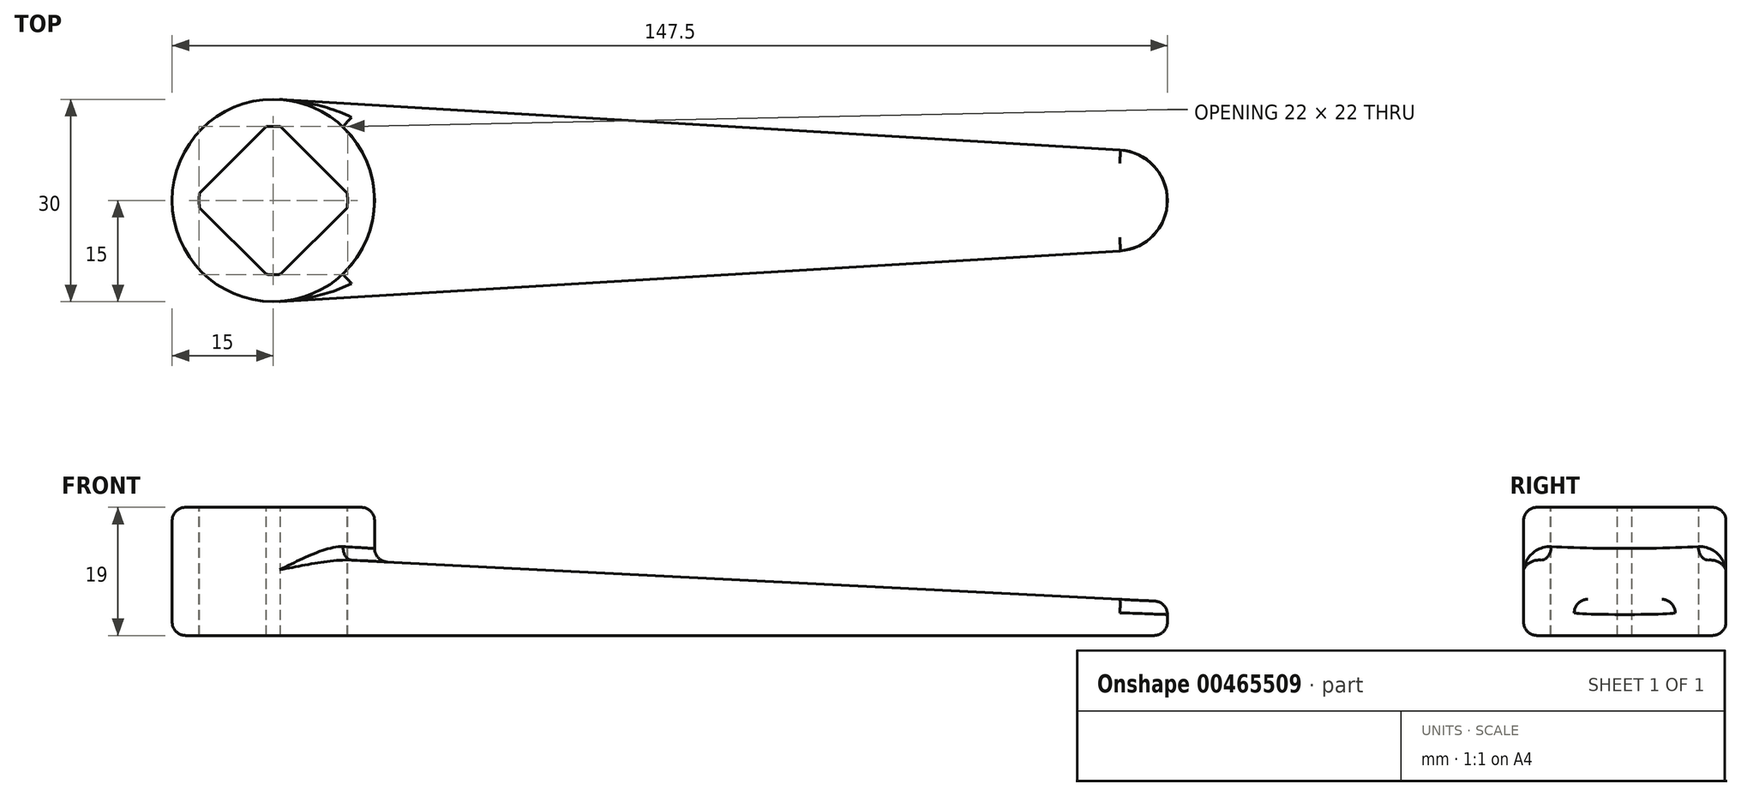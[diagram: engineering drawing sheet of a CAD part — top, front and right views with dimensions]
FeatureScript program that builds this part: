
annotation { "Feature Type Name" : "Feature", "Feature Type Description" : "" }
export const myFeature = defineFeature(function(context is Context, id is Id, definition is map)
    precondition{}
    {
        {
            var Q0;
            Q0=qCreatedBy(makeId("Top.planeOp"),FACE);
            var sketch = newSketch(context, id + "F0", { "sketchPlane" : qUnion([Q0])});
            skCircle(sketch, "E0", {"center": v(0, 0) * mm, "radius": 15 * mm});
            skLineSegment(sketch, "E1", {"start": v(0, 0) * mm, "end": v(125, 0) * mm, "construction": true});
            skCircle(sketch, "E2", {"center": v(125, 0) * mm, "radius": 7.5 * mm});
            skLineSegment(sketch, "E3", {"start": v(0.9, 14.97) * mm, "end": v(125.45, 7.49) * mm});
            skLineSegment(sketch, "E4.MirrorCS", {"start": v(0.9, -14.97) * mm, "end": v(125.45, -7.49) * mm});
            skSolve(sketch);
        }
        {
            var Q0;
            Q0 = qSketchRegion(id + "F0", true);
            extrude(context, id + "F1", {"entities" : qUnion([Q0]), "depth" : 19 * mm});
        }
        {
            var Q0;
            Q0=qCreatedBy(makeId("Front.planeOp"),FACE);
            var sketch = newSketch(context, id + "F2", { "sketchPlane" : qUnion([Q0])});
            skLineSegment(sketch, "E5.0", {"start": v(0.9, 19) * mm, "end": v(125.45, 19) * mm});
            skLineSegment(sketch, "E6.0", {"start": v(0.9, 0) * mm, "end": v(125.45, 0) * mm});
            skLineSegment(sketch, "E7", {"start": v(15, 0) * mm, "end": v(15, 19) * mm});
            skLineSegment(sketch, "E8.0", {"start": v(125.45, 19) * mm, "end": v(132.5, 19) * mm});
            skLineSegment(sketch, "E9", {"start": v(132.5, 19) * mm, "end": v(132.5, 0) * mm});
            skLineSegment(sketch, "E10.0", {"start": v(125.45, 0) * mm, "end": v(132.5, 0) * mm});
            skLineSegment(sketch, "E11", {"start": v(-15, 12.53) * mm, "end": v(132.5, 5) * mm});
            skLineSegment(sketch, "E12", {"start": v(-15, 0) * mm, "end": v(-15, 19) * mm});
            skLineSegment(sketch, "E13.0", {"start": v(0.9, 19) * mm, "end": v(-15, 19) * mm});
            skLineSegment(sketch, "E14.0", {"start": v(0.9, 0) * mm, "end": v(-15, 0) * mm});
            skPoint(sketch, "E15.orphan", {"position": v(15, 11) * mm});
            skSolve(sketch);
        }
        {
            var Q0;
            {var subQ0=sQuery(id+"F2.wireOp",EDGE,"E8.0");Q0=makeQuery(id+"F2.imprint","IMPRINT",FACE,{"disambiguationData":[TD([[makeQuery(id+"F2.imprint","IMPRINT",EDGE,{"derivedFrom":subQ0}),-1.0]])]});}
            var Q1;
            {var subQ3=sQuery(id+"F2.wireOp",EDGE,"E13.0");Q1=makeQuery(id+"F2.imprint","IMPRINT",FACE,{"disambiguationData":[TD([[makeQuery(id+"F2.imprint","IMPRINT",EDGE,{"derivedFrom":subQ3}),1.0]])]});}
            extrude(context, id + "F3", {"entities" : qUnion([Q0, Q1]), "operationType" : NewBodyOperationType.REMOVE, "oppositeDirection" : true, "depth" : 30 * mm, "symmetric" : true});
        }
        {
            var Q0;
            Q0=makeQuery(id+"F1.opExtrude","CAP_FACE",FACE,{"disambiguationData":[OSD([sQuery(id+"F0.wireOp",EDGE,"E0"),sQuery(id+"F0.wireOp",EDGE,"E2"),sQuery(id+"F0.wireOp",EDGE,"E3"),sQuery(id+"F0.wireOp",EDGE,"E4.MirrorCS")])],"isStart":true});
            var sketch = newSketch(context, id + "F4", { "sketchPlane" : qUnion([Q0])});
            skCircle(sketch, "E16", {"center": v(0, 0) * mm, "radius": 15 * mm});
            skSolve(sketch);
        }
        {
            var Q0;
            Q0 = qSketchRegion(id + "F4", true);
            extrude(context, id + "F5", {"entities" : qUnion([Q0]), "operationType" : NewBodyOperationType.ADD, "oppositeDirection" : true, "depth" : 19 * mm});
        }
        {
            var Q0;
            Q0=makeQuery(id+"F5.opExtrude","CAP_FACE",FACE,{"disambiguationData":[OSD([sQuery(id+"F4.wireOp",EDGE,"E16")])],"isStart":false});
            var sketch = newSketch(context, id + "F6", { "sketchPlane" : qUnion([Q0])});
            skCircle(sketch, "E17", {"center": v(0, 0) * mm, "radius": 11 * mm});
            skCircle(sketch, "E18.cCircle", {"center": v(0, 0) * mm, "radius": 12.02 * mm, "construction": true});
            skLineSegment(sketch, "E18.0", {"start": v(0, 12.02) * mm, "end": v(12.02, 0) * mm});
            skLineSegment(sketch, "E18.1", {"start": v(12.02, 0) * mm, "end": v(0, -12.02) * mm});
            skLineSegment(sketch, "E18.2", {"start": v(0, -12.02) * mm, "end": v(-12.02, 0) * mm});
            skLineSegment(sketch, "E18.3", {"start": v(-12.02, 0) * mm, "end": v(0, 12.02) * mm});
            skSolve(sketch);
        }
        {
            var Q0;
            {var subQ0=sQuery(id+"F6.wireOp",EDGE,"E18.0");var subQ1=sQuery(id+"F6.wireOp",EDGE,"E17");var subQ12=makeQuery(id+"F6.imprint","INTERSECT",VERTEX,{"disambiguationData":[OD(0.0)],"derivedFrom":[subQ1,subQ0]});Q0=makeQuery(id+"F6.imprint","IMPRINT",FACE,{"disambiguationData":[TD([[makeQuery(id+"F6.imprint","IMPRINT",EDGE,{"disambiguationData":[TD([[subQ12,-1.0]])],"derivedFrom":subQ1}),1.0]])]});}
            extrude(context, id + "F7", {"entities" : qUnion([Q0]), "operationType" : NewBodyOperationType.REMOVE, "endBound" : BoundingType.THROUGH_ALL, "oppositeDirection" : true, "depth" : 25 * mm});
        }
        {
            var Q0;
            Q0=makeQuery(id+"F5.opExtrude","CAP_EDGE",EDGE,{"disambiguationData":[OSD([sQuery(id+"F4.wireOp",EDGE,"E16")])],"isStart":false});
            var Q1;
            Q1=makeQuery(id+"F5.boolean.opBoolean","INTERSECT",EDGE,{"derivedFrom":[makeQuery(id+"F3.boolean.opBoolean","COPY",FACE,{"derivedFrom":makeQuery(id+"F3.opExtrude","SWEPT_FACE",FACE,{"disambiguationData":[OSD([sQuery(id+"F2.wireOp",EDGE,"E11")])]})}),makeQuery(id+"F5.opExtrude","SWEPT_FACE",FACE,{"disambiguationData":[OSD([sQuery(id+"F4.wireOp",EDGE,"E16")])]})]});
            var Q2;
            Q2=makeQuery(id+"F3.boolean.opBoolean","INTERSECT",EDGE,{"derivedFrom":[makeQuery(id+"F1.opExtrude","SWEPT_FACE",FACE,{"disambiguationData":[OSD([sQuery(id+"F0.wireOp",EDGE,"E4.MirrorCS")])]}),makeQuery(id+"F3.opExtrude","SWEPT_FACE",FACE,{"disambiguationData":[OSD([sQuery(id+"F2.wireOp",EDGE,"E11")])]})]});
            var Q3;
            Q3=makeQuery(id+"F1.opExtrude","CAP_EDGE",EDGE,{"disambiguationData":[OSD([sQuery(id+"F0.wireOp",EDGE,"E4.MirrorCS")])],"isStart":true});
            fillet(context, id + "F8", {"entities" : qUnion([Q0, Q1, Q2, Q3]), "radius" : 2 * mm, "tangentPropagation" : true, "allowEdgeOverflow" : false});
        }
    });
